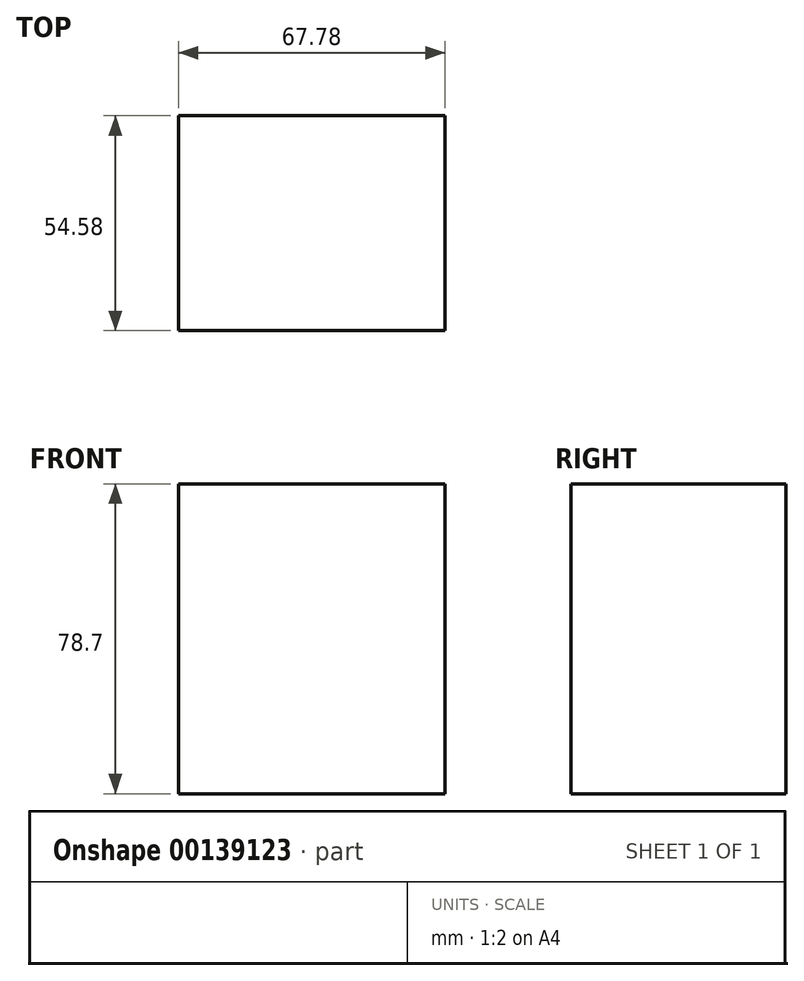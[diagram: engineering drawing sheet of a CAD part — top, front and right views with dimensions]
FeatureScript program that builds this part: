
annotation { "Feature Type Name" : "Feature", "Feature Type Description" : "" }
export const myFeature = defineFeature(function(context is Context, id is Id, definition is map)
    precondition{}
    {
        {
            var Q0;
            Q0=qCreatedBy(makeId("Front.planeOp"),FACE);
            var sketch = newSketch(context, id + "F0", { "sketchPlane" : qUnion([Q0])});
            skLineSegment(sketch, "E0.bottom", {"start": v(-33.89, 39.35) * mm, "end": v(33.89, 39.35) * mm});
            skLineSegment(sketch, "E0.top", {"start": v(-33.89, -39.35) * mm, "end": v(33.89, -39.35) * mm});
            skLineSegment(sketch, "E0.left", {"start": v(-33.89, 39.35) * mm, "end": v(-33.89, -39.35) * mm});
            skLineSegment(sketch, "E0.right", {"start": v(33.89, 39.35) * mm, "end": v(33.89, -39.35) * mm});
            skPoint(sketch, "E0.middle", {"position": v(0, 0) * mm});
            skSolve(sketch);
        }
        {
            var Q0;
            Q0 = qSketchRegion(id + "F0", true);
            extrude(context, id + "F1", {"entities" : qUnion([Q0]), "depth" : 54.58 * mm});
        }
    });
